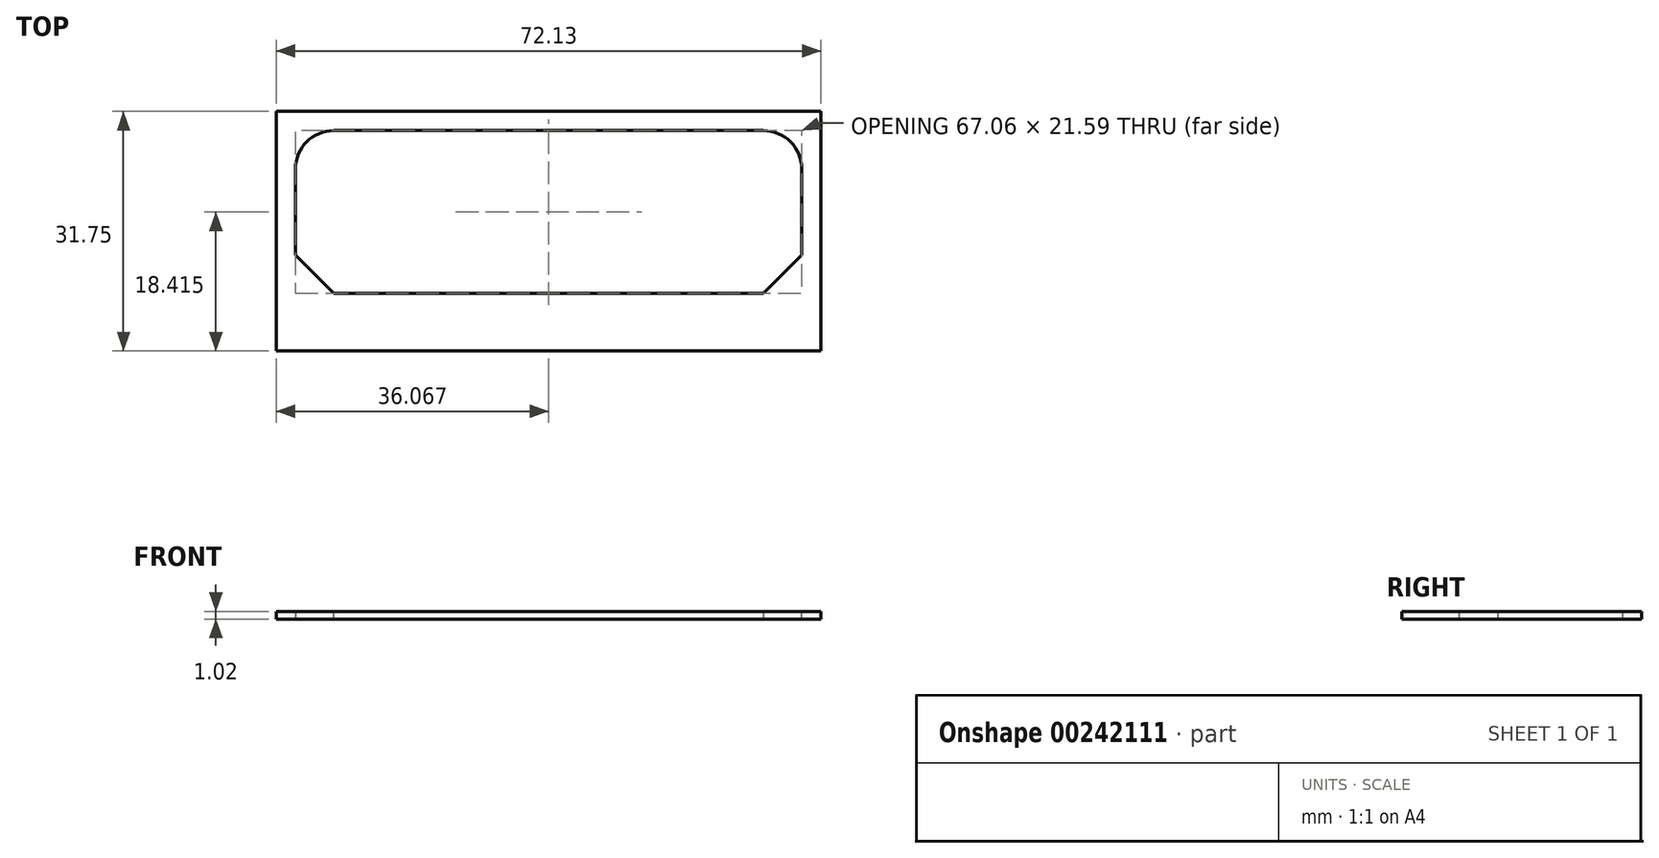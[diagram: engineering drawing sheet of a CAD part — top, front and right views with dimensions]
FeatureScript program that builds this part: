
annotation { "Feature Type Name" : "Feature", "Feature Type Description" : "" }
export const myFeature = defineFeature(function(context is Context, id is Id, definition is map)
    precondition{}
    {
        {
            var Q0;
            Q0=qCreatedBy(makeId("Top.planeOp"),FACE);
            var sketch = newSketch(context, id + "F0", { "sketchPlane" : qUnion([Q0])});
            skLineSegment(sketch, "E0.bottom", {"start": v(57.08, 11.92) * mm, "end": v(-15.05, 11.92) * mm});
            skLineSegment(sketch, "E0.top", {"start": v(57.08, -12.2) * mm, "end": v(-15.05, -12.2) * mm});
            skLineSegment(sketch, "E0.left", {"start": v(57.08, 11.92) * mm, "end": v(57.08, -12.2) * mm});
            skLineSegment(sketch, "E0.right", {"start": v(-15.05, 11.92) * mm, "end": v(-15.05, -12.2) * mm});
            skPoint(sketch, "E0.middle", {"position": v(21.02, -0.14) * mm});
            skLineSegment(sketch, "E1.bottom", {"start": v(-15.05, -12.2) * mm, "end": v(57.08, -12.2) * mm});
            skLineSegment(sketch, "E1.top", {"start": v(-15.05, -19.83) * mm, "end": v(57.08, -19.83) * mm});
            skLineSegment(sketch, "E1.left", {"start": v(-15.05, -12.2) * mm, "end": v(-15.05, -19.83) * mm});
            skLineSegment(sketch, "E1.right", {"start": v(57.08, -12.2) * mm, "end": v(57.08, -19.83) * mm});
            skLineSegment(sketch, "E2.0", {"start": v(-12.51, 9.38) * mm, "end": v(-12.51, -12.2) * mm});
            skLineSegment(sketch, "E2.1", {"start": v(54.54, 9.38) * mm, "end": v(-12.51, 9.38) * mm});
            skLineSegment(sketch, "E2.2", {"start": v(54.54, 9.38) * mm, "end": v(54.54, -12.2) * mm});
            skSolve(sketch);
        }
        {
            var Q0;
            Q0=makeQuery(id+"F0.imprint","IMPRINT",FACE,{"disambiguationData":[TD([[makeQuery(id+"F0.imprint","IMPRINT",EDGE,{"derivedFrom":sQuery(id+"F0.wireOp",EDGE,"E1.top")}),1.0]])]});
            var Q1;
            Q1=makeQuery(id+"F0.imprint","IMPRINT",FACE,{"disambiguationData":[TD([[makeQuery(id+"F0.imprint","IMPRINT",EDGE,{"derivedFrom":sQuery(id+"F0.wireOp",EDGE,"E0.bottom")}),1.0]])]});
            extrude(context, id + "F1", {"entities" : qUnion([Q0, Q1]), "depth" : 1.02 * mm});
        }
        {
            var Q0;
            Q0=makeQuery(id+"F1.opExtrude","SWEPT_EDGE",EDGE,{"disambiguationData":[OSD([sQuery(id+"F0.wireOp",EDGE,"E2.0"),sQuery(id+"F0.wireOp",EDGE,"E2.1")])]});
            var Q1;
            Q1=makeQuery(id+"F1.opExtrude","SWEPT_EDGE",EDGE,{"disambiguationData":[OSD([sQuery(id+"F0.wireOp",EDGE,"E2.1"),sQuery(id+"F0.wireOp",EDGE,"E2.2")])]});
            fillet(context, id + "F2", {"entities" : qUnion([Q0, Q1]), "radius" : 5.08 * mm, "tangentPropagation" : true, "allowEdgeOverflow" : false});
        }
        {
            var Q0;
            Q0=makeQuery(id+"F1.opExtrude","SWEPT_EDGE",EDGE,{"disambiguationData":[OSD([sQuery(id+"F0.wireOp",EDGE,"E1.bottom"),sQuery(id+"F0.wireOp",EDGE,"E2.0")])]});
            var Q1;
            Q1=makeQuery(id+"F1.opExtrude","SWEPT_EDGE",EDGE,{"disambiguationData":[OSD([sQuery(id+"F0.wireOp",EDGE,"E1.bottom"),sQuery(id+"F0.wireOp",EDGE,"E2.2")])]});
            chamfer(context, id + "F3", {"entities" : qUnion([Q0, Q1]), "width" : 5.08 * mm, "tangentPropagation" : true});
        }
    });
